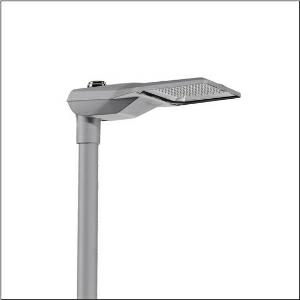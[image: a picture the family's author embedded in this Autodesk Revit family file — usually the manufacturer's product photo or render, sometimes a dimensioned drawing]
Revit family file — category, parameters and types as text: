
# Revit family: streetlight_sl_21_midi___p1_0a_5xe7a37n08mb_bed1
name_source: partatom
category: Lighting Fixtures
units: mm (PartAtom-declared; Revit-internal decimal feet)

## family parameters
Cut with Voids When Loaded = No
Host = Face
Light Source = No
Part Type = Normal
Room Calculation Point = No
Round Connector Dimension = Use Diameter
Shared = No

## types (1)
- --- (1 x LED, 18270 lm, 136 W, 3000K)
    Apparent Load = 136 VA
    CIE Flux Codes = 21 50 90 100 100
    Color Rendering = 70
    Color Temperature = 3000K
    Default Elevation = 1800 mm
    Description = Streetlight SL 21 midi, mast luminaire, primary light control with lens, of PMMA, primary optical cover: cover, of toughened safety glass, transparent, light distribution: P1.0a, light emission: direct distribution, primary light characteristic: asymmetric, installation type: side-entry, LED, 3G 2.5mm², High Power LED, rated luminous flux: 18.270lm, luminous efficacy: 134lm/W, light colour: 730, colour temperature: 3000K, control gear: NEMA (7pin), control: overheat protection, pre-setting: linear dimming characteristic, constant luminous flux control, time-dependent luminous flux control, flexible luminous flux parameterisation, mains connection: 220..240V, AC, 50/60Hz, connection cable pre-assembled, cable length: 12,5m, wiring characteristics: H05VV-F, start of lifetime: 136W, end of service life: 142W, reduction: 61W, luminaire housing, of diecast aluminium (EN AC-44300), powder-coated, Siteco® metallic grey (DB 702S), corrosivity category C5 mid according to DIN EN ISO 12944, multi-level sealing system, sealing non-destructively replaceable, inclination adjustable: 0°, 5°, 10°, 15°, length: 644mm, width: 335mm, height: 110mm, spigot size: 42mm (side-entry), mounting height: 4..8m, protection rating (complete): IP66, insulation class (complete): insulation class I (protective earthing), certification: CE, ENEC, ENEC+, VDE, impact resistance: IK10, permissible operating ambient temperature for outdoor applications: -40..+50°C, standard-compliant lighting for roads and squares, packaging unit: 1 piece

Light Distribution: P1.0a
    Height = 111 mm
    Lamp = 1 x LED
    Lamp Light Flux = 18270 lm
    Lamp Power = 136 W
    Lamp count = 1
    Length = 644 mm
    Luminous efficacy = 134 lm/W
    Manufacturer = Siteco
    ModVariant = No
    Model = 5XE7A37N08MB
    Number of Poles = 1
    OnlyDefault = Yes
    Power Factor = 1
    Product Name = Streetlight SL 21 midi | P1.0a
    Product group = mast luminaire | pylon top
    ProductGroupID = 6100
    Protection Class = Protection class I
    Protection Degree = IP 66
    RLX_Detail_Level = 1
    RLX_Emergency_Light_Flux = 0 lm
    RLX_Emergency_Type = 0
    RLX_Emergency_Type_DB = No
    RlxData = <blob elided: 37797 chars, md5=03e0ce89>
    Socket = socket
    Standby Power = 0 W
    System Light Flux = 18270 lm
    System Power = 136 W
    Type Comments = factory setting: luminous flux: 100 % | dim-lin: 254 | 695 mA
    Type Image = l_1294377.jpg
    URL = http://relux.com
    VarID = @adj_134522
    Voltage = 0 V
    Weight = 0.00 kg
    Width = 336 mm

## geometry (parser evidence)
native form markers: Blend x4, Sweep x11
no freeform markers — native parametric forms only
